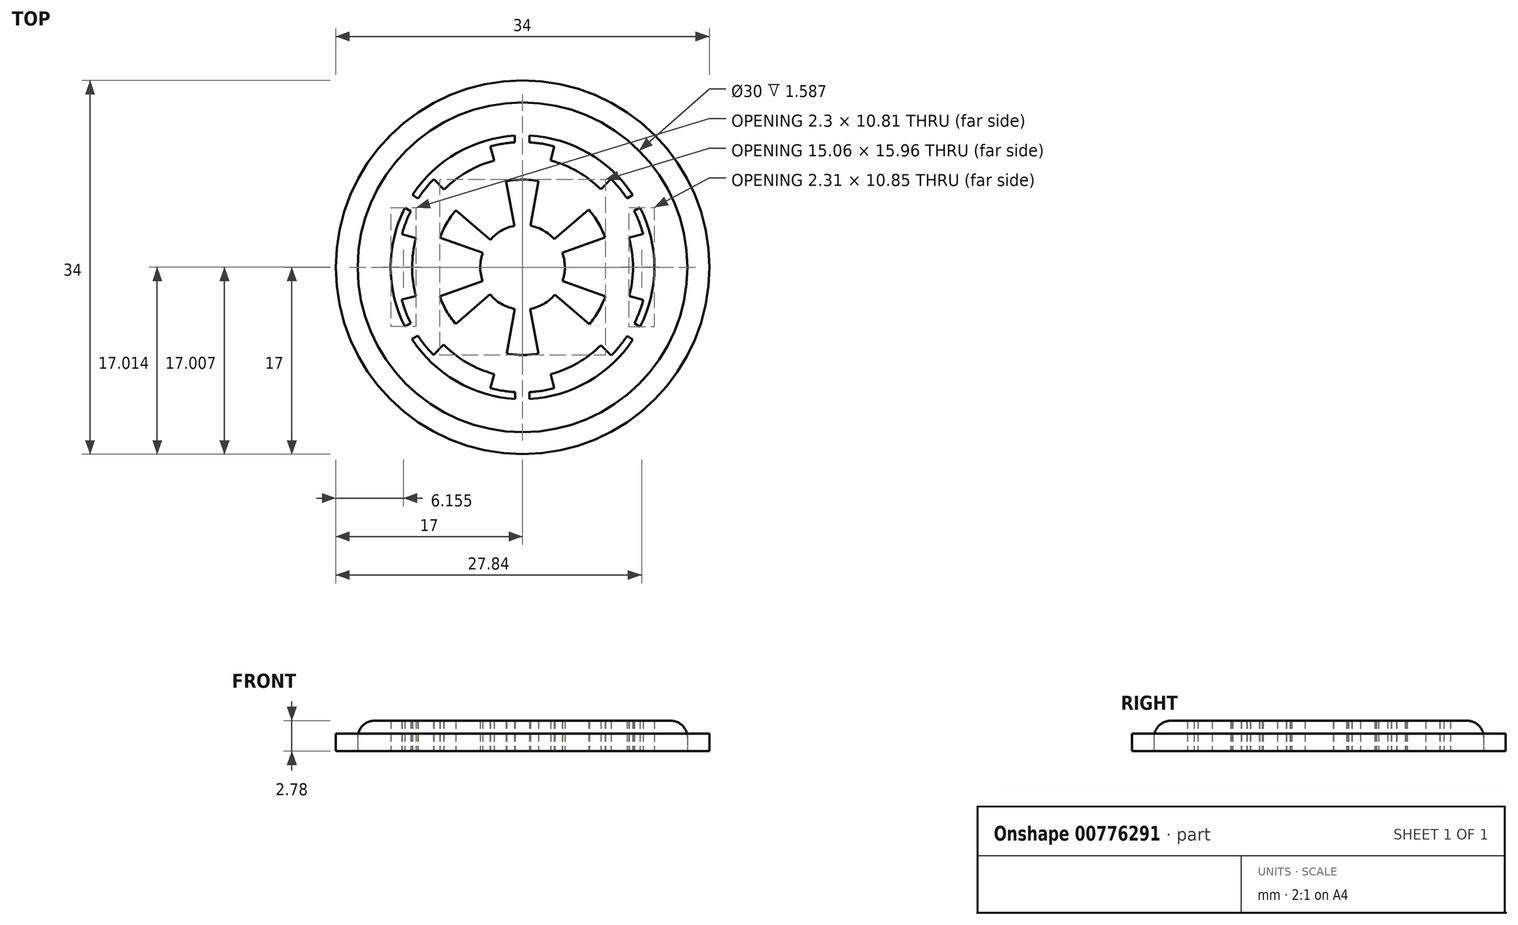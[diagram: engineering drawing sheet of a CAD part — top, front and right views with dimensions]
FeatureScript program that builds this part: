
annotation { "Feature Type Name" : "Feature", "Feature Type Description" : "" }
export const myFeature = defineFeature(function(context is Context, id is Id, definition is map)
    precondition{}
    {
        {
            assignVariable(context, id + "F0", {"name" : "InnerHeight", "anyValue" : 2.78 * mm});
        }
        {
            assignVariable(context, id + "F1", {"name" : "OutterHeight", "anyValue" : 1.59 * mm});
        }
        {
            var Q0;
            Q0=qCreatedBy(makeId("Top.planeOp"),FACE);
            var sketch = newSketch(context, id + "F2", { "sketchPlane" : qUnion([Q0])});
            skCircle(sketch, "E0", {"center": v(0, 0) * mm, "radius": 13.34 * mm});
            skSolve(sketch);
        }
        {
            var Q0;
            Q0 = qSketchRegion(id + "F2", true);
            extrude(context, id + "F3", {"entities" : qUnion([Q0]), "depth" : getVariable(context, 'InnerHeight'), "offsetDistance" : 25.4 * mm});
        }
        {
            var Q0;
            Q0=qCreatedBy(makeId("Top.planeOp"),FACE);
            var sketch = newSketch(context, id + "F4", { "sketchPlane" : qUnion([Q0])});
            skArc(sketch, "E1", {"start": v(-10.34, 3.75) * mm, "mid": v(-11, 0.08) * mm, "end": v(-10.4, -3.6) * mm});
            skArc(sketch, "E2", {"start": v(-17.31, 14.84) * mm, "mid": v(-19.71, 11.45) * mm, "end": v(-21.46, 7.7) * mm});
            skArc(sketch, "E3", {"start": v(-27.7, 7.57) * mm, "mid": v(-28.71, 0.06) * mm, "end": v(-27.73, -7.46) * mm});
            skArc(sketch, "E4", {"start": v(-29.08, 14.55) * mm, "mid": v(-30.37, 11.61) * mm, "end": v(-31.37, 8.56) * mm});
            skArc(sketch, "E5", {"start": v(-30.58, 15.48) * mm, "mid": v(-34.27, 0.04) * mm, "end": v(-30.62, -15.4) * mm});
            skCircle(sketch, "E6", {"center": v(0, 0) * mm, "radius": 38.24 * mm});
            skLineSegment(sketch, "E7", {"start": v(-8.37, 31.42) * mm, "end": v(-7.36, 27.75) * mm});
            skLineSegment(sketch, "E8", {"start": v(8.2, 31.47) * mm, "end": v(7.33, 27.76) * mm});
            skLineSegment(sketch, "E9", {"start": v(20.35, 20.25) * mm, "end": v(23, 23) * mm});
            skLineSegment(sketch, "E10", {"start": v(27.67, 7.66) * mm, "end": v(31.34, 8.67) * mm});
            skLineSegment(sketch, "E11", {"start": v(-20.43, 20.17) * mm, "end": v(-23.11, 22.87) * mm});
            skLineSegment(sketch, "E12", {"start": v(-27.7, 7.57) * mm, "end": v(-31.37, 8.56) * mm});
            skLineSegment(sketch, "E13", {"start": v(-27.73, -7.46) * mm, "end": v(-31.4, -8.43) * mm});
            skLineSegment(sketch, "E14", {"start": v(-20.5, -20.1) * mm, "end": v(-23.19, -22.8) * mm});
            skLineSegment(sketch, "E15", {"start": v(-7.34, -27.76) * mm, "end": v(-8.35, -31.43) * mm});
            skLineSegment(sketch, "E16", {"start": v(7.3, -27.77) * mm, "end": v(8.24, -31.45) * mm});
            skLineSegment(sketch, "E17", {"start": v(20.38, -20.22) * mm, "end": v(23.05, -22.94) * mm});
            skLineSegment(sketch, "E18", {"start": v(27.72, -7.48) * mm, "end": v(31.38, -8.51) * mm});
            skLineSegment(sketch, "E19", {"start": v(-4.27, 22.4) * mm, "end": v(-2.09, 10.8) * mm});
            skLineSegment(sketch, "E20", {"start": v(4.16, 22.42) * mm, "end": v(2.01, 10.81) * mm});
            skLineSegment(sketch, "E21", {"start": v(-17.31, 14.84) * mm, "end": v(-8.34, 7.17) * mm});
            skLineSegment(sketch, "E22", {"start": v(17.16, 15) * mm, "end": v(8.23, 7.3) * mm});
            skLineSegment(sketch, "E23", {"start": v(-21.46, 7.7) * mm, "end": v(-10.34, 3.75) * mm});
            skLineSegment(sketch, "E24", {"start": v(21.45, 7.73) * mm, "end": v(10.33, 3.78) * mm});
            skLineSegment(sketch, "E25.trimOffspring", {"start": v(-10.4, -3.6) * mm, "end": v(-21.51, -7.54) * mm});
            skLineSegment(sketch, "E26.trimOffspring", {"start": v(-8.44, -7.06) * mm, "end": v(-17.38, -14.76) * mm});
            skLineSegment(sketch, "E27.trimOffspring", {"start": v(8.38, -7.13) * mm, "end": v(17.34, -14.8) * mm});
            skLineSegment(sketch, "E28.trimOffspring", {"start": v(1.99, -10.82) * mm, "end": v(4.17, -22.41) * mm});
            skLineSegment(sketch, "E29.trimOffspring", {"start": v(-1.99, -10.82) * mm, "end": v(-4.13, -22.42) * mm});
            skLineSegment(sketch, "E30.trimOffspring", {"start": v(10.4, -3.6) * mm, "end": v(21.51, -7.54) * mm});
            skArc(sketch, "E31.trimOffspring", {"start": v(-8.44, -7.06) * mm, "mid": v(-5.54, -9.5) * mm, "end": v(-1.99, -10.82) * mm});
            skArc(sketch, "E32.trimOffspring", {"start": v(1.99, -10.82) * mm, "mid": v(5.5, -9.53) * mm, "end": v(8.38, -7.13) * mm});
            skArc(sketch, "E33.trimOffspring", {"start": v(-2.09, 10.8) * mm, "mid": v(-5.52, 9.51) * mm, "end": v(-8.34, 7.17) * mm});
            skArc(sketch, "E34.trimOffspring", {"start": v(8.23, 7.3) * mm, "mid": v(5.41, 9.58) * mm, "end": v(2.01, 10.81) * mm});
            skArc(sketch, "E35.trimOffspring", {"start": v(10.4, -3.6) * mm, "mid": v(11, 0.1) * mm, "end": v(10.33, 3.78) * mm});
            skArc(sketch, "E36.trimOffspring", {"start": v(4.16, 22.42) * mm, "mid": v(-0.06, 22.8) * mm, "end": v(-4.27, 22.4) * mm});
            skArc(sketch, "E37.trimOffspring", {"start": v(21.45, 7.73) * mm, "mid": v(19.65, 11.57) * mm, "end": v(17.16, 15) * mm});
            skArc(sketch, "E38.trimOffspring", {"start": v(17.34, -14.8) * mm, "mid": v(19.76, -11.36) * mm, "end": v(21.51, -7.54) * mm});
            skArc(sketch, "E39.trimOffspring", {"start": v(-4.13, -22.42) * mm, "mid": v(0.02, -22.8) * mm, "end": v(4.17, -22.41) * mm});
            skArc(sketch, "E40.trimOffspring", {"start": v(-21.51, -7.54) * mm, "mid": v(-19.78, -11.34) * mm, "end": v(-17.38, -14.76) * mm});
            skArc(sketch, "E41.trimOffspring", {"start": v(-7.36, 27.75) * mm, "mid": v(-14.4, 24.84) * mm, "end": v(-20.43, 20.17) * mm});
            skArc(sketch, "E42.trimOffspring", {"start": v(20.35, 20.25) * mm, "mid": v(14.34, 24.87) * mm, "end": v(7.33, 27.76) * mm});
            skArc(sketch, "E43.trimOffspring", {"start": v(27.72, -7.48) * mm, "mid": v(28.71, 0.1) * mm, "end": v(27.67, 7.66) * mm});
            skArc(sketch, "E44.trimOffspring", {"start": v(7.3, -27.77) * mm, "mid": v(14.35, -24.87) * mm, "end": v(20.38, -20.22) * mm});
            skArc(sketch, "E45.trimOffspring", {"start": v(-20.5, -20.1) * mm, "mid": v(-14.44, -24.82) * mm, "end": v(-7.34, -27.76) * mm});
            skLineSegment(sketch, "E46", {"start": v(-29.08, 14.55) * mm, "end": v(-30.58, 15.48) * mm});
            skLineSegment(sketch, "E47", {"start": v(-28.6, 18.88) * mm, "end": v(-27.19, 17.84) * mm});
            skLineSegment(sketch, "E48", {"start": v(-2, 34.22) * mm, "end": v(-2, 32.46) * mm});
            skLineSegment(sketch, "E49", {"start": v(1.8, 34.23) * mm, "end": v(1.8, 32.47) * mm});
            skLineSegment(sketch, "E50", {"start": v(27.14, 17.91) * mm, "end": v(28.66, 18.8) * mm});
            skLineSegment(sketch, "E51", {"start": v(29.04, 14.64) * mm, "end": v(30.56, 15.52) * mm});
            skLineSegment(sketch, "E52", {"start": v(27.19, -17.84) * mm, "end": v(28.67, -18.78) * mm});
            skLineSegment(sketch, "E53", {"start": v(29.08, -14.55) * mm, "end": v(30.58, -15.48) * mm});
            skLineSegment(sketch, "E54", {"start": v(-1.97, -32.46) * mm, "end": v(-1.97, -34.22) * mm});
            skLineSegment(sketch, "E55", {"start": v(1.81, -32.47) * mm, "end": v(1.81, -34.23) * mm});
            skLineSegment(sketch, "E56", {"start": v(-29.09, -14.53) * mm, "end": v(-30.62, -15.4) * mm});
            skLineSegment(sketch, "E57", {"start": v(-28.75, -18.66) * mm, "end": v(-27.23, -17.78) * mm});
            skArc(sketch, "E58.trimOffspring", {"start": v(-2, 32.46) * mm, "mid": v(-5.2, 32.1) * mm, "end": v(-8.37, 31.42) * mm});
            skArc(sketch, "E59.trimOffspring", {"start": v(-2, 34.22) * mm, "mid": v(-17.12, 29.7) * mm, "end": v(-28.6, 18.88) * mm});
            skArc(sketch, "E60.trimOffspring", {"start": v(27.14, 17.91) * mm, "mid": v(25.2, 20.56) * mm, "end": v(23, 23) * mm});
            skArc(sketch, "E61.trimOffspring", {"start": v(28.66, 18.8) * mm, "mid": v(17.07, 29.72) * mm, "end": v(1.8, 34.23) * mm});
            skArc(sketch, "E62.trimOffspring", {"start": v(8.2, 31.47) * mm, "mid": v(5.03, 32.13) * mm, "end": v(1.8, 32.47) * mm});
            skArc(sketch, "E63.trimOffspring", {"start": v(-23.11, 22.87) * mm, "mid": v(-25.28, 20.46) * mm, "end": v(-27.19, 17.84) * mm});
            skArc(sketch, "E64.trimOffspring", {"start": v(-31.4, -8.43) * mm, "mid": v(-30.4, -11.54) * mm, "end": v(-29.09, -14.53) * mm});
            skArc(sketch, "E65.trimOffspring", {"start": v(-8.35, -31.43) * mm, "mid": v(-5.19, -32.1) * mm, "end": v(-1.97, -32.46) * mm});
            skArc(sketch, "E66.trimOffspring", {"start": v(23.05, -22.94) * mm, "mid": v(25.25, -20.5) * mm, "end": v(27.19, -17.84) * mm});
            skArc(sketch, "E67.trimOffspring", {"start": v(31.34, 8.67) * mm, "mid": v(30.33, 11.71) * mm, "end": v(29.04, 14.64) * mm});
            skArc(sketch, "E68.trimOffspring", {"start": v(29.08, -14.55) * mm, "mid": v(30.38, -11.6) * mm, "end": v(31.38, -8.51) * mm});
            skArc(sketch, "E69.trimOffspring", {"start": v(30.58, -15.48) * mm, "mid": v(34.27, 0.02) * mm, "end": v(30.56, 15.52) * mm});
            skArc(sketch, "E70.trimOffspring", {"start": v(1.81, -32.47) * mm, "mid": v(5.05, -32.12) * mm, "end": v(8.24, -31.45) * mm});
            skArc(sketch, "E71.trimOffspring", {"start": v(1.81, -34.23) * mm, "mid": v(17.09, -29.71) * mm, "end": v(28.67, -18.78) * mm});
            skArc(sketch, "E72.trimOffspring", {"start": v(-28.75, -18.66) * mm, "mid": v(-17.22, -29.63) * mm, "end": v(-1.97, -34.22) * mm});
            skArc(sketch, "E73.trimOffspring", {"start": v(-27.23, -17.78) * mm, "mid": v(-25.33, -20.39) * mm, "end": v(-23.19, -22.8) * mm});
            skSolve(sketch);
        }
        {
            var Q0;
            Q0=qSketchRegion(id+"F4",true);
            extrude(context, id + "F5", {"entities" : qUnion([Q0]), "depth" : 8 * mm, "offsetDistance" : 25.4 * mm});
        }
        {
            var Q0;
            Q0=makeQuery(id+"F5.opExtrude","SWEPT_BODY",BODY,{"disambiguationData":[OSD([sQuery(id+"F4.wireOp",EDGE,"E1"),sQuery(id+"F4.wireOp",EDGE,"E2"),sQuery(id+"F4.wireOp",EDGE,"E3"),sQuery(id+"F4.wireOp",EDGE,"E4"),sQuery(id+"F4.wireOp",EDGE,"E5"),sQuery(id+"F4.wireOp",EDGE,"E6"),sQuery(id+"F4.wireOp",EDGE,"E7"),sQuery(id+"F4.wireOp",EDGE,"E8"),sQuery(id+"F4.wireOp",EDGE,"E9"),sQuery(id+"F4.wireOp",EDGE,"E10"),sQuery(id+"F4.wireOp",EDGE,"E11"),sQuery(id+"F4.wireOp",EDGE,"E12"),sQuery(id+"F4.wireOp",EDGE,"E13"),sQuery(id+"F4.wireOp",EDGE,"E14"),sQuery(id+"F4.wireOp",EDGE,"E15"),sQuery(id+"F4.wireOp",EDGE,"E16"),sQuery(id+"F4.wireOp",EDGE,"E17"),sQuery(id+"F4.wireOp",EDGE,"E18"),sQuery(id+"F4.wireOp",EDGE,"E19"),sQuery(id+"F4.wireOp",EDGE,"E20"),sQuery(id+"F4.wireOp",EDGE,"E21"),sQuery(id+"F4.wireOp",EDGE,"E22"),sQuery(id+"F4.wireOp",EDGE,"E23"),sQuery(id+"F4.wireOp",EDGE,"E24"),sQuery(id+"F4.wireOp",EDGE,"E25.trimOffspring"),sQuery(id+"F4.wireOp",EDGE,"E26.trimOffspring"),sQuery(id+"F4.wireOp",EDGE,"E27.trimOffspring"),sQuery(id+"F4.wireOp",EDGE,"E28.trimOffspring"),sQuery(id+"F4.wireOp",EDGE,"E29.trimOffspring"),sQuery(id+"F4.wireOp",EDGE,"E30.trimOffspring"),sQuery(id+"F4.wireOp",EDGE,"E31.trimOffspring"),sQuery(id+"F4.wireOp",EDGE,"E32.trimOffspring"),sQuery(id+"F4.wireOp",EDGE,"E33.trimOffspring"),sQuery(id+"F4.wireOp",EDGE,"E34.trimOffspring"),sQuery(id+"F4.wireOp",EDGE,"E35.trimOffspring"),sQuery(id+"F4.wireOp",EDGE,"E36.trimOffspring"),sQuery(id+"F4.wireOp",EDGE,"E37.trimOffspring"),sQuery(id+"F4.wireOp",EDGE,"E38.trimOffspring"),sQuery(id+"F4.wireOp",EDGE,"E39.trimOffspring"),sQuery(id+"F4.wireOp",EDGE,"E40.trimOffspring"),sQuery(id+"F4.wireOp",EDGE,"E41.trimOffspring"),sQuery(id+"F4.wireOp",EDGE,"E42.trimOffspring"),sQuery(id+"F4.wireOp",EDGE,"E43.trimOffspring"),sQuery(id+"F4.wireOp",EDGE,"E44.trimOffspring"),sQuery(id+"F4.wireOp",EDGE,"E45.trimOffspring"),sQuery(id+"F4.wireOp",EDGE,"E46"),sQuery(id+"F4.wireOp",EDGE,"E47"),sQuery(id+"F4.wireOp",EDGE,"E48"),sQuery(id+"F4.wireOp",EDGE,"E49"),sQuery(id+"F4.wireOp",EDGE,"E50"),sQuery(id+"F4.wireOp",EDGE,"E51"),sQuery(id+"F4.wireOp",EDGE,"E52"),sQuery(id+"F4.wireOp",EDGE,"E53"),sQuery(id+"F4.wireOp",EDGE,"E54"),sQuery(id+"F4.wireOp",EDGE,"E55"),sQuery(id+"F4.wireOp",EDGE,"E56"),sQuery(id+"F4.wireOp",EDGE,"E57"),sQuery(id+"F4.wireOp",EDGE,"E58.trimOffspring"),sQuery(id+"F4.wireOp",EDGE,"E59.trimOffspring"),sQuery(id+"F4.wireOp",EDGE,"E60.trimOffspring"),sQuery(id+"F4.wireOp",EDGE,"E61.trimOffspring"),sQuery(id+"F4.wireOp",EDGE,"E62.trimOffspring"),sQuery(id+"F4.wireOp",EDGE,"E63.trimOffspring"),sQuery(id+"F4.wireOp",EDGE,"E64.trimOffspring"),sQuery(id+"F4.wireOp",EDGE,"E65.trimOffspring"),sQuery(id+"F4.wireOp",EDGE,"E66.trimOffspring"),sQuery(id+"F4.wireOp",EDGE,"E67.trimOffspring"),sQuery(id+"F4.wireOp",EDGE,"E68.trimOffspring"),sQuery(id+"F4.wireOp",EDGE,"E69.trimOffspring"),sQuery(id+"F4.wireOp",EDGE,"E70.trimOffspring"),sQuery(id+"F4.wireOp",EDGE,"E71.trimOffspring"),sQuery(id+"F4.wireOp",EDGE,"E72.trimOffspring"),sQuery(id+"F4.wireOp",EDGE,"E73.trimOffspring")])]});
            var Q1;
            Q1=qCreatedBy(makeId("Origin.pointOp"),VERTEX);
            transform(context, id + "F6", {"entities" : qUnion([Q0]), "transformType" : TransformType.SCALE_UNIFORMLY, "scale" : .35, "scalePoint" : qUnion([Q1]), "makeCopy" : false});
        }
        {
            var Q0;
            Q0=makeQuery(id+"F5.opExtrude","SWEPT_BODY",BODY,{"disambiguationData":[OSD([sQuery(id+"F4.wireOp",EDGE,"E1"),sQuery(id+"F4.wireOp",EDGE,"E2"),sQuery(id+"F4.wireOp",EDGE,"E3"),sQuery(id+"F4.wireOp",EDGE,"E4"),sQuery(id+"F4.wireOp",EDGE,"E5"),sQuery(id+"F4.wireOp",EDGE,"E6"),sQuery(id+"F4.wireOp",EDGE,"E7"),sQuery(id+"F4.wireOp",EDGE,"E8"),sQuery(id+"F4.wireOp",EDGE,"E9"),sQuery(id+"F4.wireOp",EDGE,"E10"),sQuery(id+"F4.wireOp",EDGE,"E11"),sQuery(id+"F4.wireOp",EDGE,"E12"),sQuery(id+"F4.wireOp",EDGE,"E13"),sQuery(id+"F4.wireOp",EDGE,"E14"),sQuery(id+"F4.wireOp",EDGE,"E15"),sQuery(id+"F4.wireOp",EDGE,"E16"),sQuery(id+"F4.wireOp",EDGE,"E17"),sQuery(id+"F4.wireOp",EDGE,"E18"),sQuery(id+"F4.wireOp",EDGE,"E19"),sQuery(id+"F4.wireOp",EDGE,"E20"),sQuery(id+"F4.wireOp",EDGE,"E21"),sQuery(id+"F4.wireOp",EDGE,"E22"),sQuery(id+"F4.wireOp",EDGE,"E23"),sQuery(id+"F4.wireOp",EDGE,"E24"),sQuery(id+"F4.wireOp",EDGE,"E25.trimOffspring"),sQuery(id+"F4.wireOp",EDGE,"E26.trimOffspring"),sQuery(id+"F4.wireOp",EDGE,"E27.trimOffspring"),sQuery(id+"F4.wireOp",EDGE,"E28.trimOffspring"),sQuery(id+"F4.wireOp",EDGE,"E29.trimOffspring"),sQuery(id+"F4.wireOp",EDGE,"E30.trimOffspring"),sQuery(id+"F4.wireOp",EDGE,"E31.trimOffspring"),sQuery(id+"F4.wireOp",EDGE,"E32.trimOffspring"),sQuery(id+"F4.wireOp",EDGE,"E33.trimOffspring"),sQuery(id+"F4.wireOp",EDGE,"E34.trimOffspring"),sQuery(id+"F4.wireOp",EDGE,"E35.trimOffspring"),sQuery(id+"F4.wireOp",EDGE,"E36.trimOffspring"),sQuery(id+"F4.wireOp",EDGE,"E37.trimOffspring"),sQuery(id+"F4.wireOp",EDGE,"E38.trimOffspring"),sQuery(id+"F4.wireOp",EDGE,"E39.trimOffspring"),sQuery(id+"F4.wireOp",EDGE,"E40.trimOffspring"),sQuery(id+"F4.wireOp",EDGE,"E41.trimOffspring"),sQuery(id+"F4.wireOp",EDGE,"E42.trimOffspring"),sQuery(id+"F4.wireOp",EDGE,"E43.trimOffspring"),sQuery(id+"F4.wireOp",EDGE,"E44.trimOffspring"),sQuery(id+"F4.wireOp",EDGE,"E45.trimOffspring"),sQuery(id+"F4.wireOp",EDGE,"E46"),sQuery(id+"F4.wireOp",EDGE,"E47"),sQuery(id+"F4.wireOp",EDGE,"E48"),sQuery(id+"F4.wireOp",EDGE,"E49"),sQuery(id+"F4.wireOp",EDGE,"E50"),sQuery(id+"F4.wireOp",EDGE,"E51"),sQuery(id+"F4.wireOp",EDGE,"E52"),sQuery(id+"F4.wireOp",EDGE,"E53"),sQuery(id+"F4.wireOp",EDGE,"E54"),sQuery(id+"F4.wireOp",EDGE,"E55"),sQuery(id+"F4.wireOp",EDGE,"E56"),sQuery(id+"F4.wireOp",EDGE,"E57"),sQuery(id+"F4.wireOp",EDGE,"E58.trimOffspring"),sQuery(id+"F4.wireOp",EDGE,"E59.trimOffspring"),sQuery(id+"F4.wireOp",EDGE,"E60.trimOffspring"),sQuery(id+"F4.wireOp",EDGE,"E61.trimOffspring"),sQuery(id+"F4.wireOp",EDGE,"E62.trimOffspring"),sQuery(id+"F4.wireOp",EDGE,"E63.trimOffspring"),sQuery(id+"F4.wireOp",EDGE,"E64.trimOffspring"),sQuery(id+"F4.wireOp",EDGE,"E65.trimOffspring"),sQuery(id+"F4.wireOp",EDGE,"E66.trimOffspring"),sQuery(id+"F4.wireOp",EDGE,"E67.trimOffspring"),sQuery(id+"F4.wireOp",EDGE,"E68.trimOffspring"),sQuery(id+"F4.wireOp",EDGE,"E69.trimOffspring"),sQuery(id+"F4.wireOp",EDGE,"E70.trimOffspring"),sQuery(id+"F4.wireOp",EDGE,"E71.trimOffspring"),sQuery(id+"F4.wireOp",EDGE,"E72.trimOffspring"),sQuery(id+"F4.wireOp",EDGE,"E73.trimOffspring")])]});
            var Q1;
            Q1=makeQuery(id+"F3.opExtrude","SWEPT_BODY",BODY,{"disambiguationData":[OSD([sQuery(id+"F2.wireOp",EDGE,"E0")])]});
            booleanBodies(context, id + "F7", {"operationType" : BooleanOperationType.SUBTRACTION, "tools" : qUnion([Q0]), "targets" : qUnion([Q1])});
        }
        {
            var Q0;
            Q0=qCreatedBy(makeId("Top.planeOp"),FACE);
            var sketch = newSketch(context, id + "F8", { "sketchPlane" : qUnion([Q0])});
            skCircle(sketch, "E74", {"center": v(0, 0) * mm, "radius": 15 * mm});
            skCircle(sketch, "E75", {"center": v(0, 0) * mm, "radius": 17 * mm});
            skSolve(sketch);
        }
        {
            var Q0;
            Q0 = qSketchRegion(id + "F8", true);
            extrude(context, id + "F9", {"entities" : qUnion([Q0]), "depth" : getVariable(context, 'OutterHeight'), "offsetDistance" : 25.4 * mm});
        }
        {
            var Q0;
            Q0=makeQuery(id+"F8.imprint","IMPRINT",FACE,{"disambiguationData":[TD([[makeQuery(id+"F8.imprint","IMPRINT",EDGE,{"derivedFrom":sQuery(id+"F8.wireOp",EDGE,"E74")}),1.0]])]});
            extrude(context, id + "F10", {"entities" : qUnion([Q0]), "depth" : getVariable(context, 'InnerHeight'), "offsetDistance" : 25.4 * mm});
        }
        {
            var Q0;
            Q0=makeQuery(id+"F7.opBoolean","SPLIT",BODY,{"disambiguationData":[OD(2.0)],"derivedFrom":makeQuery(id+"F3.opExtrude","SWEPT_BODY",BODY,{"disambiguationData":[OSD([sQuery(id+"F2.wireOp",EDGE,"E0")])]})});
            var Q1;
            Q1=makeQuery(id+"F7.opBoolean","SPLIT",BODY,{"disambiguationData":[OD(0.0)],"derivedFrom":makeQuery(id+"F3.opExtrude","SWEPT_BODY",BODY,{"disambiguationData":[OSD([sQuery(id+"F2.wireOp",EDGE,"E0")])]})});
            var Q2;
            Q2=makeQuery(id+"F7.opBoolean","SPLIT",BODY,{"disambiguationData":[OD(3.0)],"derivedFrom":makeQuery(id+"F3.opExtrude","SWEPT_BODY",BODY,{"disambiguationData":[OSD([sQuery(id+"F2.wireOp",EDGE,"E0")])]})});
            var Q3;
            Q3=makeQuery(id+"F7.opBoolean","SPLIT",BODY,{"disambiguationData":[OD(4.0)],"derivedFrom":makeQuery(id+"F3.opExtrude","SWEPT_BODY",BODY,{"disambiguationData":[OSD([sQuery(id+"F2.wireOp",EDGE,"E0")])]})});
            var Q4;
            Q4=makeQuery(id+"F7.opBoolean","SPLIT",BODY,{"disambiguationData":[OD(1.0)],"derivedFrom":makeQuery(id+"F3.opExtrude","SWEPT_BODY",BODY,{"disambiguationData":[OSD([sQuery(id+"F2.wireOp",EDGE,"E0")])]})});
            var Q5;
            Q5=makeQuery(id+"F7.opBoolean","SPLIT",BODY,{"disambiguationData":[OD(5.0)],"derivedFrom":makeQuery(id+"F3.opExtrude","SWEPT_BODY",BODY,{"disambiguationData":[OSD([sQuery(id+"F2.wireOp",EDGE,"E0")])]})});
            var Q6;
            Q6=makeQuery(id+"F7.opBoolean","SPLIT",BODY,{"disambiguationData":[OD(6.0)],"derivedFrom":makeQuery(id+"F3.opExtrude","SWEPT_BODY",BODY,{"disambiguationData":[OSD([sQuery(id+"F2.wireOp",EDGE,"E0")])]})});
            var Q7;
            Q7=makeQuery(id+"F10.opExtrude","SWEPT_BODY",BODY,{"disambiguationData":[OSD([sQuery(id+"F8.wireOp",EDGE,"E74")])]});
            booleanBodies(context, id + "F11", {"operationType" : BooleanOperationType.SUBTRACTION, "tools" : qUnion([Q0, Q1, Q2, Q3, Q4, Q5, Q6]), "targets" : qUnion([Q7])});
        }
        {
            var Q0;
            Q0=makeQuery(id+"F10.opExtrude","CAP_EDGE",EDGE,{"disambiguationData":[OSD([sQuery(id+"F8.wireOp",EDGE,"E74")])],"isStart":false});
            fillet(context, id + "F12", {"entities" : qUnion([Q0]), "radius" : 1.53 * mm, "tangentPropagation" : true, "allowEdgeOverflow" : false});
        }
    });
